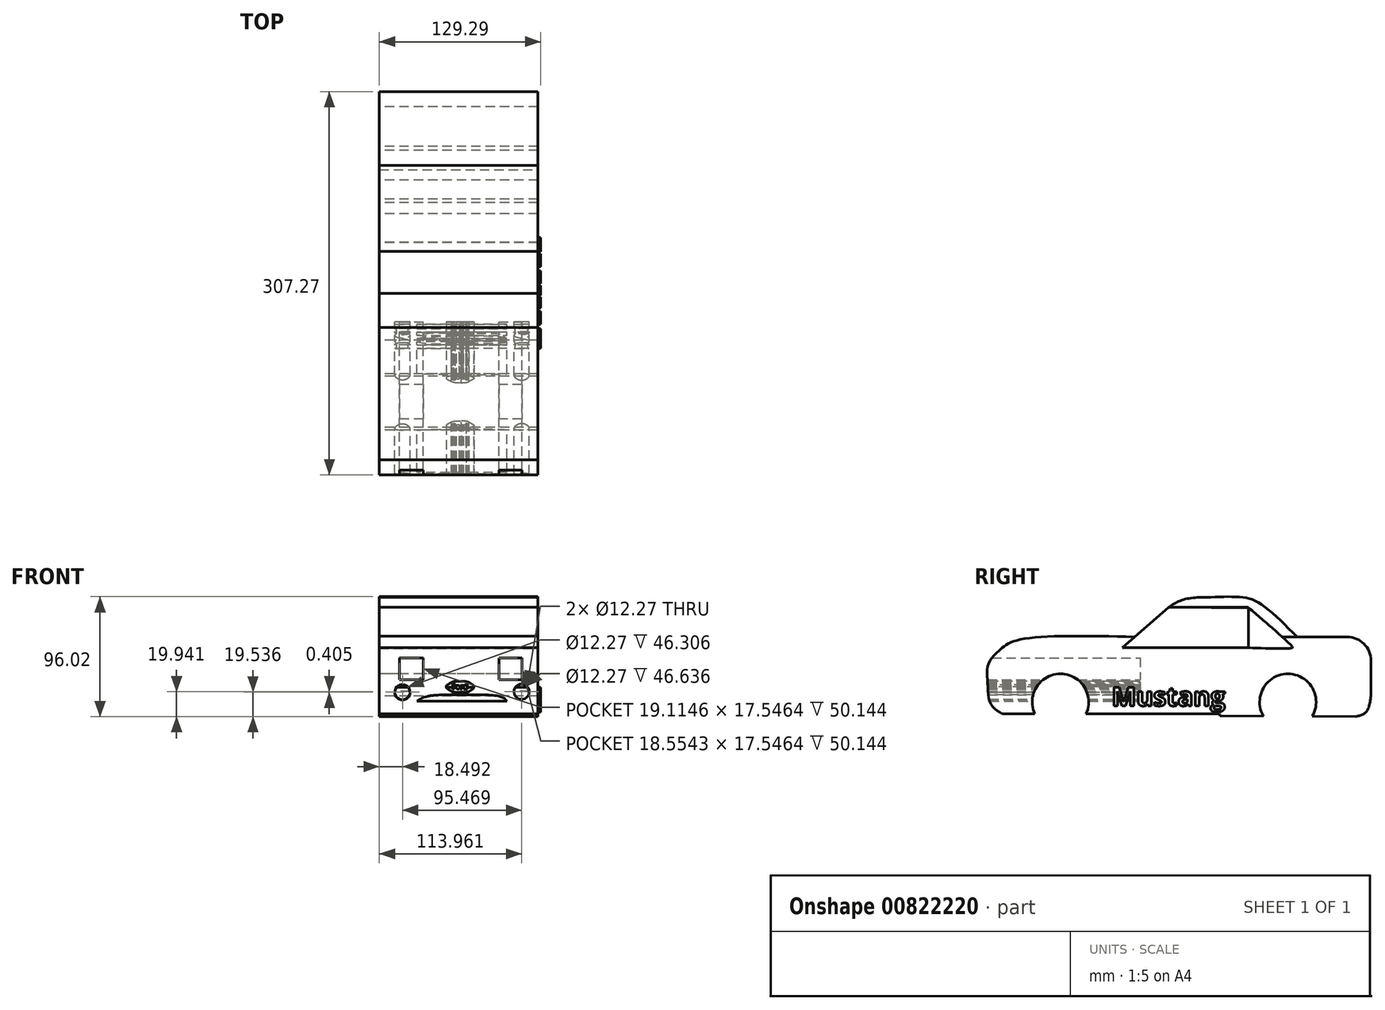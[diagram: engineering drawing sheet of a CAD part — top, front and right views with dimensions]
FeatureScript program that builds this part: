
annotation { "Feature Type Name" : "Feature", "Feature Type Description" : "" }
export const myFeature = defineFeature(function(context is Context, id is Id, definition is map)
    precondition{}
    {
        {
            var Q0;
            Q0=qCreatedBy(makeId("Right.planeOp"),FACE);
            var sketch = newSketch(context, id + "F0", { "sketchPlane" : qUnion([Q0])});
            skLineSegment(sketch, "E0.bottom", {"start": v(-14.51, 12.7) * mm, "end": v(63.5, 12.7) * mm});
            skPoint(sketch, "E0.middle", {"position": v(0, 0) * mm});
            skLineSegment(sketch, "E1.bottom", {"start": v(57.01, 44.8) * mm, "end": v(86.62, 44.8) * mm});
            skLineSegment(sketch, "E1.top", {"start": v(57.01, 45.24) * mm, "end": v(86.62, 45.24) * mm});
            skLineSegment(sketch, "E1.left", {"start": v(57.01, 44.8) * mm, "end": v(57.01, 45.24) * mm});
            skLineSegment(sketch, "E1.right", {"start": v(86.62, 44.8) * mm, "end": v(86.62, 45.24) * mm});
            skLineSegment(sketch, "E2", {"start": v(63.5, 12.7) * mm, "end": v(86.62, 12.7) * mm});
            skFitSpline(sketch, "E3", {"points": [v(86.62, 44.8) * mm, v(121.6, 13.54) * mm, v(121.6, 12.7) * mm, v(86.62, 12.7) * mm], "startDerivative": vector(98.37, -84.17) * mm, "endDerivative": vector(-114.26, 4.16) * mm});
            skLineSegment(sketch, "E4", {"start": v(57.01, 45.24) * mm, "end": v(22.77, 45.24) * mm});
            skLineSegment(sketch, "E5", {"start": v(22.77, 45.24) * mm, "end": v(-14.51, 12.7) * mm});
            skFitSpline(sketch, "E6", {"points": [v(-110.48, 12.7) * mm, v(-97.65, 19.03) * mm, v(-4.53, 21.41) * mm], "startDerivative": vector(33.75, 25.18) * mm, "endDerivative": vector(159.8, -3.57) * mm});
            skPoint(sketch, "E0.left.end.orphan", {"position": v(-63.5, -12.7) * mm});
            skPoint(sketch, "E7.orphan", {"position": v(-63.5, 12.7) * mm});
            skPoint(sketch, "E0.right.end.orphan", {"position": v(63.5, -12.7) * mm});
            skLineSegment(sketch, "E8", {"start": v(113.6, 21.41) * mm, "end": v(165.57, 21.41) * mm});
            skLineSegment(sketch, "E9", {"start": v(86.62, 45.24) * mm, "end": v(86.62, 12.7) * mm});
            skLineSegment(sketch, "E10", {"start": v(63.5, 12.7) * mm, "end": v(63.5, -40.26) * mm});
            skLineSegment(sketch, "E11", {"start": v(63.5, -40.26) * mm, "end": v(-43.48, -40.26) * mm});
            skPoint(sketch, "E12.end.orphan", {"position": v(187.06, -52.96) * mm});
            skLineSegment(sketch, "E13", {"start": v(63.73, -41.8) * mm, "end": v(98.48, -42) * mm});
            skCircle(sketch, "E14", {"center": v(-64.03, -30.8) * mm, "radius": 22.62 * mm});
            skLineSegment(sketch, "E15.trimOffspring", {"start": v(-84.57, -40.26) * mm, "end": v(-110.48, -40.26) * mm});
            skCircle(sketch, "E16", {"center": v(118.13, -30.8) * mm, "radius": 22.62 * mm});
            skPoint(sketch, "E16.centerSnap0", {"position": v(118.13, -42.12) * mm});
            skLineSegment(sketch, "E17.trimOffspring", {"start": v(137.65, -42.23) * mm, "end": v(172.48, -42.42) * mm});
            skFitSpline(sketch, "E18", {"points": [v(56.4, 53.26) * mm, v(80.23, 53.26) * mm, v(95.51, 48.37) * mm, v(125.46, 21.41) * mm], "startDerivative": vector(79.83, 2.78) * mm, "endDerivative": vector(77.47, -78.14) * mm});
            skPoint(sketch, "E19.1.internal.orphan", {"position": v(43.55, 53.26) * mm});
            skPoint(sketch, "E19.2.internal.orphan", {"position": v(35.6, 53.26) * mm});
            skPoint(sketch, "E19.3.internal.orphan", {"position": v(30.1, 53.26) * mm});
            skPoint(sketch, "E20.visualSharp", {"position": v(184.62, 21.41) * mm});
            skArc(sketch, "E20.filletArc", {"start": v(184.62, 2.36) * mm, "mid": v(179.04, 15.83) * mm, "end": v(165.57, 21.41) * mm});
            skPoint(sketch, "E21.end.orphan", {"position": v(184.62, -52.96) * mm});
            skLineSegment(sketch, "E22", {"start": v(184.62, 2.36) * mm, "end": v(184.62, -25.97) * mm});
            skPoint(sketch, "E23.visualSharp", {"position": v(172.53, -42.42) * mm});
            skArc(sketch, "E23.filletArc", {"start": v(172.48, -42.42) * mm, "mid": v(172.53, -42.42) * mm, "end": v(172.58, -42.42) * mm});
            skFitSpline(sketch, "E24", {"points": [v(172.58, -42.42) * mm, v(180.91, -38.55) * mm, v(184.62, -25.97) * mm], "startDerivative": vector(20.89, 5.17) * mm, "endDerivative": vector(3.7, 27.07) * mm});
            skPoint(sketch, "E25.start.orphan", {"position": v(184.62, -42.42) * mm});
            skFitSpline(sketch, "E26", {"points": [v(22.7, 45.18) * mm, v(34.68, 51.37) * mm, v(56.44, 53.26) * mm], "startDerivative": vector(24.66, 16.41) * mm, "endDerivative": vector(42.1, 0.4) * mm});
            skFitSpline(sketch, "E27", {"points": [v(-110.48, -40.26) * mm, v(-119.84, -32.11) * mm, v(-122.26, -15.16) * mm, v(-121.51, 0) * mm, v(-110.48, 12.7) * mm], "startDerivative": vector(-49.45, 29.3) * mm, "endDerivative": vector(52.58, 45.84) * mm});
            skFitSpline(sketch, "E28", {"points": [v(63.73, -41.8) * mm, v(63.5, -40.26) * mm], "startDerivative": vector(-0.23, 1.55) * mm, "endDerivative": vector(-0.23, 1.55) * mm});
            skSolve(sketch);
        }
        {
            var Q0;
            {var subQ1=sQuery(id+"F0.wireOp",EDGE,"E0.bottom");Q0=makeQuery(id+"F0.imprint","IMPRINT",FACE,{"disambiguationData":[TD([[makeQuery(id+"F0.imprint","IMPRINT",EDGE,{"derivedFrom":subQ1}),-1.0]])]});}
            extrude(context, id + "F1", {"entities" : qUnion([Q0]), "depth" : 127 * mm, "offsetDistance" : 25.4 * mm});
        }
        {
            var Q0;
            {var subQ11=sQuery(id+"F0.wireOp",EDGE,"E1.top");Q0=makeQuery(id+"F0.imprint","IMPRINT",FACE,{"disambiguationData":[TD([[makeQuery(id+"F0.imprint","IMPRINT",EDGE,{"derivedFrom":subQ11}),1.0]])]});}
            extrude(context, id + "F2", {"entities" : qUnion([Q0]), "depth" : 127 * mm, "offsetDistance" : 25.4 * mm});
        }
        {
            var Q0;
            {var subQ5=sQuery(id+"F0.wireOp",EDGE,"E0.bottom");Q0=makeQuery(id+"F0.imprint","IMPRINT",FACE,{"disambiguationData":[TD([[makeQuery(id+"F0.imprint","IMPRINT",EDGE,{"derivedFrom":subQ5}),1.0]])]});}
            extrude(context, id + "F3", {"entities" : qUnion([Q0]), "depth" : 127 * mm, "offsetDistance" : 25.4 * mm});
        }
        {
            var Q0;
            {var subQ1=sQuery(id+"F0.wireOp",EDGE,"E3");var subQ3=makeQuery(id+"F0.imprint","INTERSECT",VERTEX,{"derivedFrom":[subQ1,sQuery(id+"F0.wireOp",EDGE,"E8")]});Q0=makeQuery(id+"F0.imprint","IMPRINT",FACE,{"disambiguationData":[TD([[makeQuery(id+"F0.imprint","IMPRINT",EDGE,{"disambiguationData":[TD([[subQ3,1.0]])],"derivedFrom":subQ1}),-1.0]])]});}
            extrude(context, id + "F4", {"entities" : qUnion([Q0]), "depth" : 127 * mm, "offsetDistance" : 25.4 * mm});
        }
        {
            var Q0;
            {var subQ1=sQuery(id+"F0.wireOp",EDGE,"E2");Q0=makeQuery(id+"F0.imprint","IMPRINT",FACE,{"disambiguationData":[TD([[makeQuery(id+"F0.imprint","IMPRINT",EDGE,{"derivedFrom":subQ1}),-1.0]])]});}
            extrude(context, id + "F5", {"entities" : qUnion([Q0]), "depth" : 127 * mm, "offsetDistance" : 25.4 * mm});
        }
        {
            var Q0;
            Q0=qCreatedBy(makeId("Front.planeOp"),FACE);
            var sketch = newSketch(context, id + "F6", { "sketchPlane" : qUnion([Q0])});
            skLineSegment(sketch, "E29", {"start": v(0, 4.6) * mm, "end": v(35.33, 4.6) * mm});
            skLineSegment(sketch, "E30", {"start": v(35.33, 4.6) * mm, "end": v(35.33, -12.95) * mm});
            skLineSegment(sketch, "E31", {"start": v(35.33, -12.95) * mm, "end": v(0, -12.95) * mm});
            skLineSegment(sketch, "E32", {"start": v(127.06, 4.6) * mm, "end": v(95.66, 4.6) * mm});
            skLineSegment(sketch, "E33", {"start": v(95.66, 4.6) * mm, "end": v(95.66, -12.95) * mm});
            skLineSegment(sketch, "E34", {"start": v(95.66, -12.95) * mm, "end": v(131, -12.95) * mm});
            skFitSpline(sketch, "E35", {"points": [v(95.66, 4.6) * mm, v(89.45, 0) * mm, v(81.61, -12.82) * mm], "startDerivative": vector(-15.16, -8.7) * mm, "endDerivative": vector(-13.05, -25.22) * mm});
            skFitSpline(sketch, "E36", {"points": [v(35.33, 4.6) * mm, v(41.45, 0) * mm, v(48.47, -12.9) * mm], "startDerivative": vector(15.13, -8.6) * mm, "endDerivative": vector(11.36, -25.47) * mm});
            skLineSegment(sketch, "E37", {"start": v(16.21, 4.6) * mm, "end": v(16.21, -12.95) * mm});
            skLineSegment(sketch, "E38", {"start": v(114.22, 4.6) * mm, "end": v(114.22, -12.95) * mm});
            skCircle(sketch, "E39", {"center": v(18.5, -22.88) * mm, "radius": 6.13 * mm});
            skCircle(sketch, "E40", {"center": v(113.96, -22.48) * mm, "radius": 6.13 * mm});
            skLineSegment(sketch, "E41", {"start": v(38.44, -30.22) * mm, "end": v(102.3, -30.22) * mm});
            skLineSegment(sketch, "E42", {"start": v(38.44, -30.22) * mm, "end": v(30.12, -30.22) * mm});
            skFitSpline(sketch, "E43", {"points": [v(30.12, -30.22) * mm, v(37.62, -26.4) * mm, v(66.4, -25.06) * mm], "startDerivative": vector(17.3, 12.32) * mm, "endDerivative": vector(51.84, -0.77) * mm});
            skFitSpline(sketch, "E44", {"points": [v(102.3, -30.22) * mm, v(97.97, -26.75) * mm, v(66.4, -25.06) * mm], "startDerivative": vector(-10.14, 12.87) * mm, "endDerivative": vector(-55.21, -0.78) * mm});
            skLineSegment(sketch, "E45.left", {"start": v(75.84, -18.64) * mm, "end": v(75.84, -18.6) * mm});
            skPoint(sketch, "E45.middle", {"position": v(64.67, -18.6) * mm});
            skFitSpline(sketch, "E46", {"points": [v(57.72, -15.09) * mm, v(53.5, -18.6) * mm, v(57.73, -22.1) * mm], "startDerivative": vector(-12.66, -7.02) * mm, "endDerivative": vector(12.69, -7) * mm});
            skFitSpline(sketch, "E47", {"points": [v(71.8, -15.09) * mm, v(75.84, -18.6) * mm, v(72.16, -22.1) * mm], "startDerivative": vector(11.88, -6.88) * mm, "endDerivative": vector(-11.26, -7.15) * mm});
            skPoint(sketch, "E48.orphan", {"position": v(53.5, -15.09) * mm});
            skPoint(sketch, "E45.right.start.orphan", {"position": v(53.5, -22.1) * mm});
            skPoint(sketch, "E49.orphan", {"position": v(75.84, -15.09) * mm});
            skPoint(sketch, "E50.orphan", {"position": v(75.84, -22.1) * mm});
            skFitSpline(sketch, "E51", {"points": [v(57.72, -15.09) * mm, v(59.15, -14.4) * mm, v(65.58, -14.12) * mm], "startDerivative": vector(3.44, 2.36) * mm, "endDerivative": vector(11.4, -0.14) * mm});
            skFitSpline(sketch, "E52", {"points": [v(71.8, -15.09) * mm, v(70.36, -14.55) * mm, v(65.58, -14.12) * mm], "startDerivative": vector(-3.35, 1.64) * mm, "endDerivative": vector(-8.6, 0.41) * mm});
            skFitSpline(sketch, "E53", {"points": [v(57.73, -22.1) * mm, v(58.56, -22.78) * mm, v(64.17, -23.13) * mm], "startDerivative": vector(1.92, -2.5) * mm, "endDerivative": vector(9.91, 0.1) * mm});
            skFitSpline(sketch, "E54", {"points": [v(72.16, -22.1) * mm, v(71.05, -22.75) * mm, v(64.17, -23.13) * mm], "startDerivative": vector(-2.74, -2.4) * mm, "endDerivative": vector(-12.02, 0) * mm});
            skText(sketch, "E55", { "text": "Ford", "fontName": "OpenSans-Bold.ttf"});
            skPoint(sketch, "E56.MirrorCS.end.orphan", {"position": v(-10.96, -12.82) * mm});
            skPoint(sketch, "E56.MirrorCS.start.orphan", {"position": v(-25, 4.6) * mm});
            const initialGuessF6  = {"E55": [0.05822, -0.0204, 1, 0, 0.004]};
            skSetInitialGuess(sketch, initialGuessF6);
            skSolve(sketch);
        }
        {
            var Q0;
            Q0 = qSketchRegion(id + "F6", true);
            var Q1;
            Q1 = qConstructionFilter(qBodyType(qCreatedBy(id + "F6" ,EDGE), BodyType.WIRE), ConstructionObject.NO);
            extrude(context, id + "F7", {"entities" : qUnion([Q0]), "operationType" : NewBodyOperationType.REMOVE, "surfaceEntities" : qUnion([Q1]), "depth" : 125.73 * mm, "offsetDistance" : 25.4 * mm});
        }
        {
            var Q0;
            Q0=qCreatedBy(makeId("Right.planeOp"),FACE);
            var sketch = newSketch(context, id + "F8", { "sketchPlane" : qUnion([Q0])});
            skText(sketch, "E57", { "text": "Mustang", "fontName": "OpenSans-Bold.ttf"});
            const initialGuessF8  = {"E57": [-0.02304, -0.03384, 1, 0, 0.01503]};
            skSetInitialGuess(sketch, initialGuessF8);
            skSolve(sketch);
        }
        {
            var Q0;
            Q0 = qSketchRegion(id + "F8", true);
            extrude(context, id + "F9", {"entities" : qUnion([Q0]), "operationType" : NewBodyOperationType.ADD, "depth" : 129.29 * mm, "offsetDistance" : 25.4 * mm});
        }
    });
